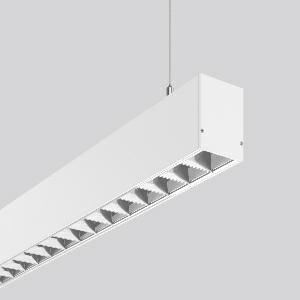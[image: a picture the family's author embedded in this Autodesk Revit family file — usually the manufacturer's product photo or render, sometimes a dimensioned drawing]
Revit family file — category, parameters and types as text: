
# Revit family: less_is_more_50_312345_002_1_76_bda9
name_source: partatom
category: Lighting Fixtures
units: mm (PartAtom-declared; Revit-internal decimal feet)

## family parameters
Cut with Voids When Loaded = No
Host = Face
Light Source = No
Part Type = Normal
Room Calculation Point = No
Round Connector Dimension = Use Diameter
Shared = No

## types (1)
- LESS IS MORE 50 (1 x LED Modul 840, 9250 lm, 4000)
    Apparent Load = 76 VA
    CIE Flux Codes = 95 100 100 63 100
    Color Rendering = 80
    Color Temperature = 4000
    Default Elevation = 1800 mm
    Description = Series: LESS IS MORE 50
Linear pendant luminaire for aesthetically sophisticated lighting. Housing: extruded aluminium profile, powder-coated. End cap aluminium powder-coated. Canopy made of aluminium, powder-coated. Alea optical system: Reflector structure (ABS, Aluminium-coated, highly polished) with integrated diffuser made of non-yellowing plastic (PMMA) opal for glare-free light at the workstation (screen-compliant according to EN 12464-1). Direct 65%, indirect 35% light emission. Controlled separately. Suitable for pendant. 2-point steel cable suspension freely positionable and infinitely height-adjustable. Special lengths available on request. LED unit with integrated converter interchangeable and removable. Suitable for through-wiring. With sensors or as a safety luminaire on request. 
Colour: traffic white, matt (RAL 9016)
Length: 1967 mm
Width: 57 mm
Height: 75 mm
Suspension length: 2000 mm
Lamp: LED
Socket: without socket
Colour temperature: 4000K
Colour rendering index (CRI): 80
Light source: LED
Socket lamp2: Without base
Colour temperature: 4000K
System power: 76 W
Rated luminous flux: 9250 lm
Luminous efficiency: 122 lm/W
Control gear: Converter, dimmable, DALI
Control gear: Converter, dimmable, DALI
Protection class: I
Type of protection: IP 20
    Height = 75 mm
    Lamp = 1 x LED Modul 840
    Lamp Light Flux = 9250 lm
    Lamp count = 1
    Length = 1967 mm
    Lifetime = 50000 h
    Luminous efficacy = 122 lm/W
    Manufacturer = RZB
    ModVariant = No
    Model = 312345.002.1.76
    Mounting Place = Ceiling
    Mounting Type = Pendant
    Number of Poles = 1
    OnlyDefault = Yes
    Power Factor = 1
    Product Name = LESS IS MORE 50
    Product group = Pendant LED linear luminaires
    ProductGroupID = 907
    Protection Class = Protection class I
    Protection Degree = IP 20
    RLX_Detail_Level = 1
    RLX_Emergency_Light_Flux = 0 lm
    RLX_Emergency_Type = 0
    RLX_Emergency_Type_DB = No
    RlxData = <blob elided: 37489 chars, md5=b8a35dd4>
    Socket = socket
    Standby Power = 0 W
    System Light Flux = 9250 lm
    System Power = 76 W
    Type Comments = Product without accessories
    Type Image = 312342.002.jpg
    URL = http://relux.com
    VarID = ---
    Voltage = 230 V
    Voltage Range = 220-240 V
    Weight = 0.00 kg
    Width = 57 mm

## geometry (parser evidence)
native form markers: Blend x4, Sweep x13
no freeform markers — native parametric forms only
